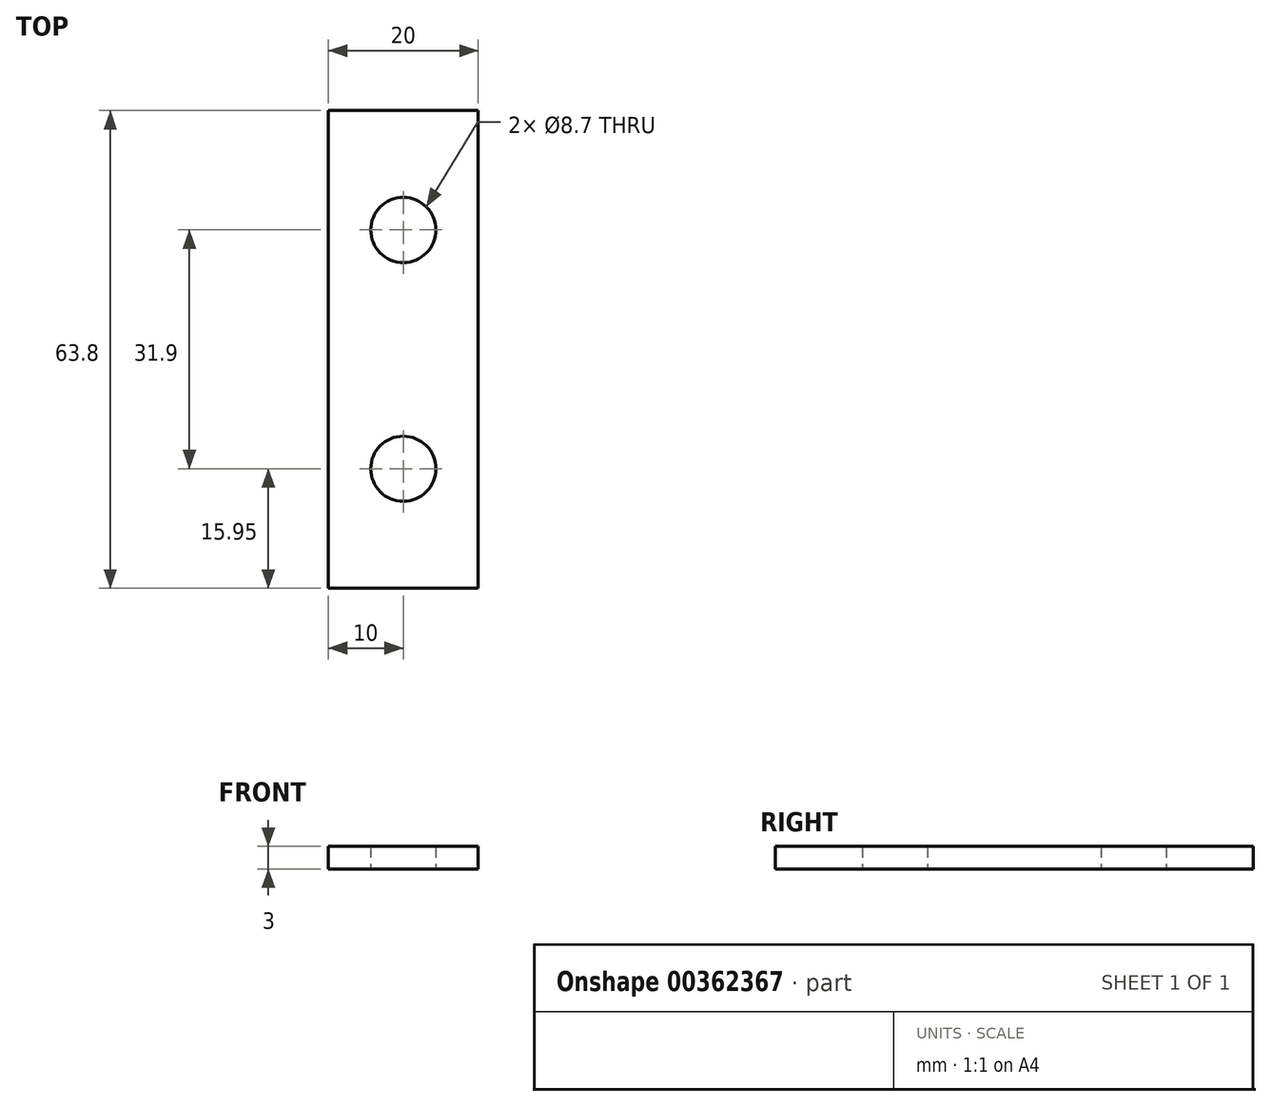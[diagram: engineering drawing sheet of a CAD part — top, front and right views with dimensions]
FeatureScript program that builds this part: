
annotation { "Feature Type Name" : "Feature", "Feature Type Description" : "" }
export const myFeature = defineFeature(function(context is Context, id is Id, definition is map)
    precondition{}
    {
        {
            var Q0;
            Q0=qCreatedBy(makeId("Top.planeOp"),FACE);
            var sketch = newSketch(context, id + "F0", { "sketchPlane" : qUnion([Q0])});
            skLineSegment(sketch, "E0.bottom", {"start": v(10, 31.9) * mm, "end": v(-10, 31.9) * mm});
            skLineSegment(sketch, "E0.top", {"start": v(10, -31.9) * mm, "end": v(-10, -31.9) * mm});
            skLineSegment(sketch, "E0.left", {"start": v(10, 31.9) * mm, "end": v(10, -31.9) * mm});
            skLineSegment(sketch, "E0.right", {"start": v(-10, 31.9) * mm, "end": v(-10, -31.9) * mm});
            skPoint(sketch, "E0.middle", {"position": v(0, 0) * mm});
            skCircle(sketch, "E1", {"center": v(0, 15.95) * mm, "radius": 4.35 * mm});
            skCircle(sketch, "E2", {"center": v(0, -15.95) * mm, "radius": 4.35 * mm});
            skSolve(sketch);
        }
        {
            var Q0;
            Q0=makeQuery(id+"F0.imprint","IMPRINT",FACE,{"disambiguationData":[TD([[makeQuery(id+"F0.imprint","IMPRINT",EDGE,{"derivedFrom":sQuery(id+"F0.wireOp",EDGE,"E0.bottom")}),1.0]])]});
            extrude(context, id + "F1", {"entities" : qUnion([Q0]), "depth" : 3 * mm});
        }
    });
